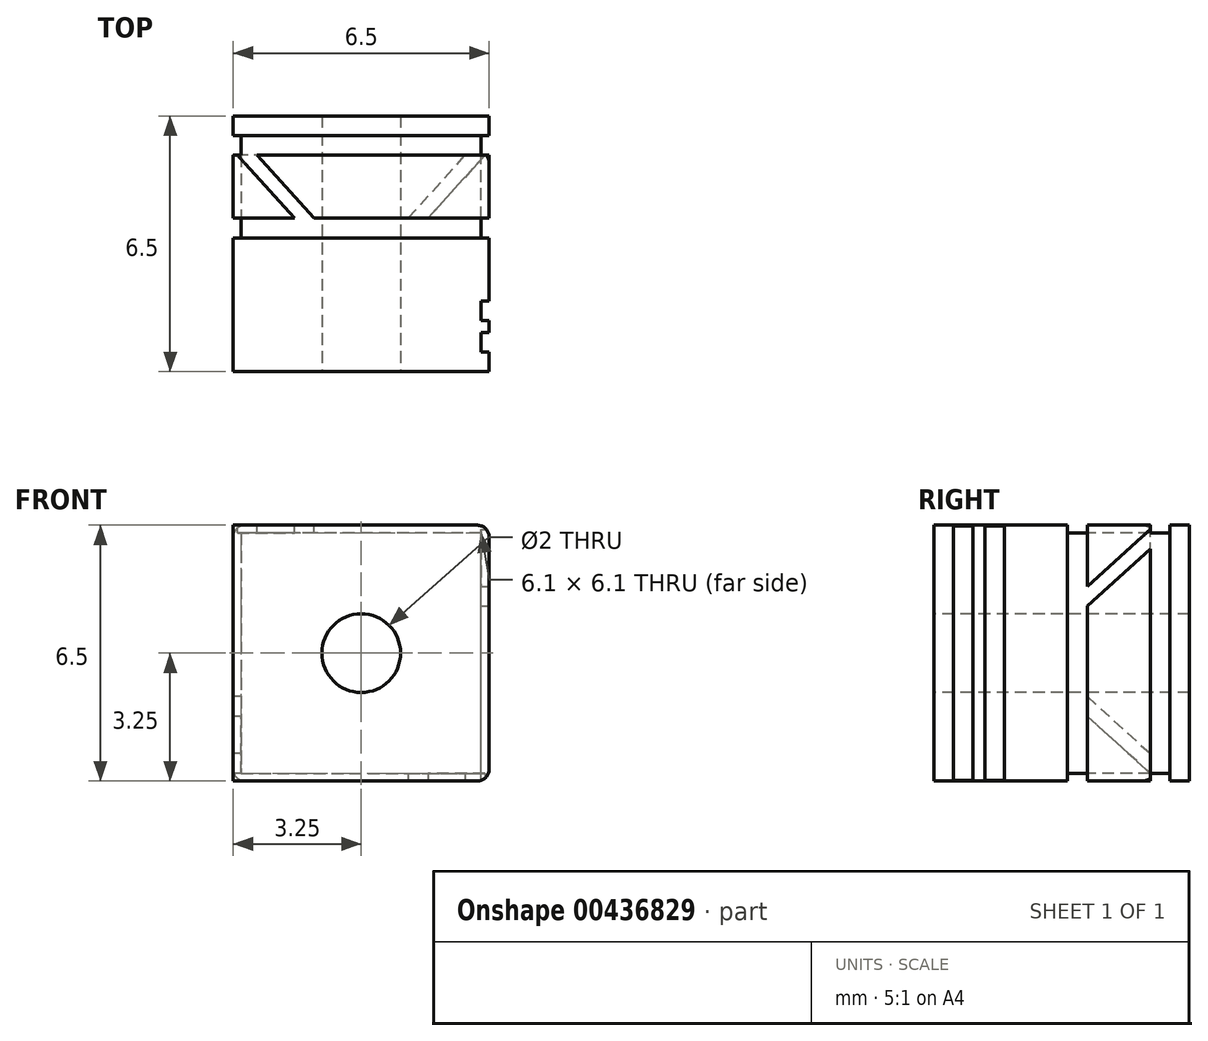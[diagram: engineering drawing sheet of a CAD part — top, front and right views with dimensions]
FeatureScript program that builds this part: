
annotation { "Feature Type Name" : "Feature", "Feature Type Description" : "" }
export const myFeature = defineFeature(function(context is Context, id is Id, definition is map)
    precondition{}
    {
        {
            var Q0;
            Q0=qCreatedBy(makeId("Front.planeOp"),FACE);
            var sketch = newSketch(context, id + "F0", { "sketchPlane" : qUnion([Q0])});
            skLineSegment(sketch, "E0.bottom", {"start": v(0, 0) * mm, "end": v(6.5, 0) * mm});
            skLineSegment(sketch, "E0.top", {"start": v(0, -6.5) * mm, "end": v(6.5, -6.5) * mm});
            skLineSegment(sketch, "E0.left", {"start": v(0, 0) * mm, "end": v(0, -6.5) * mm});
            skLineSegment(sketch, "E0.right", {"start": v(6.5, 0) * mm, "end": v(6.5, -6.5) * mm});
            skSolve(sketch);
        }
        {
            var Q0;
            Q0=makeQuery(id+"F0.imprint","IMPRINT",FACE,{"disambiguationData":[TD([[makeQuery(id+"F0.imprint","IMPRINT",EDGE,{"derivedFrom":sQuery(id+"F0.wireOp",EDGE,"E0.bottom")}),-1.0]])]});
            extrude(context, id + "F1", {"entities" : qUnion([Q0]), "depth" : 6.5 * mm});
        }
        {
            var Q0;
            Q0=makeQuery(id+"F1.opExtrude","CAP_FACE",FACE,{"disambiguationData":[OSD([sQuery(id+"F0.wireOp",EDGE,"E0.bottom"),sQuery(id+"F0.wireOp",EDGE,"E0.top"),sQuery(id+"F0.wireOp",EDGE,"E0.left"),sQuery(id+"F0.wireOp",EDGE,"E0.right")])],"isStart":false});
            var sketch = newSketch(context, id + "F2", { "sketchPlane" : qUnion([Q0])});
            skCircle(sketch, "E1", {"center": v(3.25, -3.25) * mm, "radius": 1 * mm});
            skPoint(sketch, "E1.centerSnap0", {"position": v(3.25, -6.5) * mm});
            skPoint(sketch, "E1.centerSnap1", {"position": v(0, -3.25) * mm});
            skLineSegment(sketch, "E2", {"start": v(0.3, 0) * mm, "end": v(0.3, -6.5) * mm});
            skLineSegment(sketch, "E3", {"start": v(0.45, -6.5) * mm, "end": v(0.45, 0) * mm});
            skSolve(sketch);
        }
        {
            var Q0;
            Q0=makeQuery(id+"F2.imprint","IMPRINT",FACE,{"disambiguationData":[TD([[makeQuery(id+"F2.imprint","IMPRINT",EDGE,{"derivedFrom":sQuery(id+"F2.wireOp",EDGE,"E1")}),1.0]])]});
            extrude(context, id + "F3", {"entities" : qUnion([Q0]), "operationType" : NewBodyOperationType.REMOVE, "oppositeDirection" : true, "depth" : 25 * mm});
        }
        {
            var Q0;
            Q0=makeQuery(id+"F1.opExtrude","SWEPT_FACE",FACE,{"disambiguationData":[OSD([sQuery(id+"F0.wireOp",EDGE,"E0.right")])]});
            var sketch = newSketch(context, id + "F4", { "sketchPlane" : qUnion([Q0])});
            skLineSegment(sketch, "E4", {"start": v(-6, -6.5) * mm, "end": v(-6, 0) * mm});
            skLineSegment(sketch, "E5", {"start": v(-0.5, -6.5) * mm, "end": v(-0.5, 0) * mm});
            skLineSegment(sketch, "E6.bottom", {"start": v(-5.5, -6.5) * mm, "end": v(-5.2, -6.5) * mm});
            skLineSegment(sketch, "E6.top", {"start": v(-5.5, 0) * mm, "end": v(-5.2, 0) * mm});
            skLineSegment(sketch, "E6.left", {"start": v(-5.5, -6.5) * mm, "end": v(-5.5, 0) * mm});
            skLineSegment(sketch, "E6.right", {"start": v(-5.2, -6.5) * mm, "end": v(-5.2, 0) * mm});
            skLineSegment(sketch, "E7.bottom", {"start": v(-4.7, -6.5) * mm, "end": v(-3.1, -6.5) * mm});
            skLineSegment(sketch, "E7.top", {"start": v(-4.7, 0) * mm, "end": v(-3.1, 0) * mm});
            skLineSegment(sketch, "E7.left", {"start": v(-4.7, -6.5) * mm, "end": v(-4.7, 0) * mm});
            skLineSegment(sketch, "E7.right", {"start": v(-3.1, -6.5) * mm, "end": v(-3.1, 0) * mm});
            skLineSegment(sketch, "E8.bottom", {"start": v(-2.6, -6.5) * mm, "end": v(-1, -6.5) * mm});
            skLineSegment(sketch, "E8.top", {"start": v(-2.6, 0) * mm, "end": v(-1, 0) * mm});
            skLineSegment(sketch, "E8.left", {"start": v(-2.6, -6.5) * mm, "end": v(-2.6, -2.06) * mm});
            skLineSegment(sketch, "E8.right", {"start": v(-1, -6.5) * mm, "end": v(-1, -0.6) * mm});
            skLineSegment(sketch, "E9", {"start": v(-1, -0.1) * mm, "end": v(-2.6, -1.56) * mm});
            skLineSegment(sketch, "E10", {"start": v(-2.6, -2.06) * mm, "end": v(-1, -0.6) * mm});
            skLineSegment(sketch, "E11.trimOffspring", {"start": v(-2.6, -1.56) * mm, "end": v(-2.6, 0) * mm});
            skLineSegment(sketch, "E12.trimOffspring", {"start": v(-1, -0.1) * mm, "end": v(-1, 0) * mm});
            skSolve(sketch);
        }
        {
            var Q0;
            {var subQ0=sQuery(id+"F4.wireOp",EDGE,"E4");Q0=makeQuery(id+"F4.imprint","IMPRINT",FACE,{"disambiguationData":[TD([[makeQuery(id+"F4.imprint","IMPRINT",EDGE,{"derivedFrom":subQ0}),-1.0]])]});}
            var Q1;
            {var subQ0=sQuery(id+"F4.wireOp",EDGE,"E6.right");Q1=makeQuery(id+"F4.imprint","IMPRINT",FACE,{"disambiguationData":[TD([[makeQuery(id+"F4.imprint","IMPRINT",EDGE,{"derivedFrom":subQ0}),-1.0]])]});}
            var Q2;
            {var subQ6=sQuery(id+"F4.wireOp",EDGE,"E5");Q2=makeQuery(id+"F4.imprint","IMPRINT",FACE,{"disambiguationData":[TD([[makeQuery(id+"F4.imprint","IMPRINT",EDGE,{"derivedFrom":subQ6}),1.0]])]});}
            extrude(context, id + "F5", {"entities" : qUnion([Q0, Q1, Q2]), "operationType" : NewBodyOperationType.REMOVE, "oppositeDirection" : true, "depth" : 0.2 * mm});
        }
        {
            var Q0;
            Q0=makeQuery(id+"F1.opExtrude","SWEPT_FACE",FACE,{"disambiguationData":[OSD([sQuery(id+"F0.wireOp",EDGE,"E0.bottom")])]});
            var sketch = newSketch(context, id + "F6", { "sketchPlane" : qUnion([Q0])});
            skLineSegment(sketch, "E13", {"start": v(6.5, -6) * mm, "end": v(0, -6) * mm});
            skLineSegment(sketch, "E14", {"start": v(6.5, -0.5) * mm, "end": v(0, -0.5) * mm});
            skLineSegment(sketch, "E15.bottom", {"start": v(6.5, -5.5) * mm, "end": v(6.5, -5.2) * mm});
            skLineSegment(sketch, "E15.top", {"start": v(0, -5.5) * mm, "end": v(0, -5.2) * mm});
            skLineSegment(sketch, "E15.left", {"start": v(6.5, -5.5) * mm, "end": v(0, -5.5) * mm});
            skLineSegment(sketch, "E15.right", {"start": v(6.5, -5.2) * mm, "end": v(0, -5.2) * mm});
            skLineSegment(sketch, "E16.bottom", {"start": v(6.5, -4.7) * mm, "end": v(6.5, -3.1) * mm});
            skLineSegment(sketch, "E16.top", {"start": v(0, -4.7) * mm, "end": v(0, -3.1) * mm});
            skLineSegment(sketch, "E16.left", {"start": v(6.5, -4.7) * mm, "end": v(0, -4.7) * mm});
            skLineSegment(sketch, "E16.right", {"start": v(6.5, -3.1) * mm, "end": v(0, -3.1) * mm});
            skLineSegment(sketch, "E17.bottom", {"start": v(6.5, -2.6) * mm, "end": v(6.5, -1) * mm});
            skLineSegment(sketch, "E17.top", {"start": v(0, -2.6) * mm, "end": v(0, -1) * mm});
            skLineSegment(sketch, "E17.left", {"start": v(6.5, -2.6) * mm, "end": v(2.06, -2.6) * mm});
            skLineSegment(sketch, "E17.right", {"start": v(6.5, -1) * mm, "end": v(0.6, -1) * mm});
            skLineSegment(sketch, "E18", {"start": v(0.1, -1) * mm, "end": v(1.56, -2.6) * mm});
            skLineSegment(sketch, "E19", {"start": v(2.06, -2.6) * mm, "end": v(0.6, -1) * mm});
            skLineSegment(sketch, "E20.trimOffspring", {"start": v(1.56, -2.6) * mm, "end": v(0, -2.6) * mm});
            skLineSegment(sketch, "E21.trimOffspring", {"start": v(0.1, -1) * mm, "end": v(0, -1) * mm});
            skSolve(sketch);
        }
        {
            var Q0;
            {var subQ1=sQuery(id+"F0.wireOp",EDGE,"E0.right");var subQ2=sQuery(id+"F0.wireOp",EDGE,"E0.bottom");var subQ3=makeQuery(id+"F1.opExtrude","SWEPT_EDGE",EDGE,{"disambiguationData":[OSD([subQ2,subQ1])]});var subQ4=makeQuery(id+"F5.boolean.opBoolean","COPY",EDGE,{"derivedFrom":makeQuery(id+"F5.opExtrude","CAP_EDGE",EDGE,{"disambiguationData":[OSD([subQ2,subQ1]),TDD([makeQuery(id+"F4.imprint","IMPRINT",EDGE,{"disambiguationData":[TD([[makeQuery(id+"F4.imprint","INTERSECT",VERTEX,{"derivedFrom":[subQ3,sQuery(id+"F4.wireOp",EDGE,"E4")]}),-1.0]])],"derivedFrom":subQ3})])],"isStart":false})});Q0=makeQuery(id+"F6.imprint","IMPRINT",FACE,{"disambiguationData":[TD([[makeQuery(id+"F6.imprint","IMPRINT",EDGE,{"derivedFrom":subQ4}),1.0]])]});}
            var Q1;
            {var subQ1=sQuery(id+"F0.wireOp",EDGE,"E0.right");var subQ2=sQuery(id+"F0.wireOp",EDGE,"E0.bottom");var subQ3=makeQuery(id+"F1.opExtrude","SWEPT_EDGE",EDGE,{"disambiguationData":[OSD([subQ2,subQ1])]});var subQ4=makeQuery(id+"F5.boolean.opBoolean","COPY",EDGE,{"derivedFrom":makeQuery(id+"F5.opExtrude","CAP_EDGE",EDGE,{"disambiguationData":[OSD([subQ2,subQ1]),TDD([makeQuery(id+"F4.imprint","IMPRINT",EDGE,{"disambiguationData":[TD([[makeQuery(id+"F4.imprint","INTERSECT",VERTEX,{"derivedFrom":[subQ3,sQuery(id+"F4.wireOp",EDGE,"E6.top"),sQuery(id+"F4.wireOp",EDGE,"E6.right")]}),-1.0]])],"derivedFrom":subQ3})])],"isStart":false})});Q1=makeQuery(id+"F6.imprint","IMPRINT",FACE,{"disambiguationData":[TD([[makeQuery(id+"F6.imprint","IMPRINT",EDGE,{"derivedFrom":subQ4}),1.0]])]});}
            var Q2;
            Q2=makeQuery(id+"F6.imprint","IMPRINT",FACE,{"disambiguationData":[TD([[makeQuery(id+"F6.imprint","IMPRINT",EDGE,{"derivedFrom":sQuery(id+"F6.wireOp",EDGE,"E18")}),1.0]])]});
            extrude(context, id + "F7", {"entities" : qUnion([Q0, Q1, Q2]), "operationType" : NewBodyOperationType.REMOVE, "oppositeDirection" : true, "depth" : 0.2 * mm});
        }
        {
            var Q0;
            Q0=makeQuery(id+"F1.opExtrude","SWEPT_FACE",FACE,{"disambiguationData":[OSD([sQuery(id+"F0.wireOp",EDGE,"E0.left")])]});
            var sketch = newSketch(context, id + "F8", { "sketchPlane" : qUnion([Q0])});
            skLineSegment(sketch, "E22", {"start": v(6, 0) * mm, "end": v(6, -6.5) * mm});
            skLineSegment(sketch, "E23", {"start": v(0.5, 0) * mm, "end": v(0.5, -6.5) * mm});
            skLineSegment(sketch, "E24.bottom", {"start": v(5.5, 0) * mm, "end": v(5.2, 0) * mm});
            skLineSegment(sketch, "E24.top", {"start": v(5.5, -6.5) * mm, "end": v(5.2, -6.5) * mm});
            skLineSegment(sketch, "E24.left", {"start": v(5.5, 0) * mm, "end": v(5.5, -6.5) * mm});
            skLineSegment(sketch, "E24.right", {"start": v(5.2, 0) * mm, "end": v(5.2, -6.5) * mm});
            skLineSegment(sketch, "E25.bottom", {"start": v(4.7, 0) * mm, "end": v(3.1, 0) * mm});
            skLineSegment(sketch, "E25.top", {"start": v(4.7, -6.5) * mm, "end": v(3.1, -6.5) * mm});
            skLineSegment(sketch, "E25.left", {"start": v(4.7, 0) * mm, "end": v(4.7, -6.5) * mm});
            skLineSegment(sketch, "E25.right", {"start": v(3.1, 0) * mm, "end": v(3.1, -6.5) * mm});
            skLineSegment(sketch, "E26.bottom", {"start": v(2.6, 0) * mm, "end": v(1, 0) * mm});
            skLineSegment(sketch, "E26.top", {"start": v(2.6, -6.5) * mm, "end": v(1, -6.5) * mm});
            skLineSegment(sketch, "E26.left", {"start": v(2.6, 0) * mm, "end": v(2.6, -4.35) * mm});
            skLineSegment(sketch, "E26.right", {"start": v(1, 0) * mm, "end": v(1, -5.8) * mm});
            skLineSegment(sketch, "E27", {"start": v(1, -6.3) * mm, "end": v(2.6, -4.85) * mm});
            skLineSegment(sketch, "E28", {"start": v(2.6, -4.35) * mm, "end": v(1, -5.8) * mm});
            skLineSegment(sketch, "E29.trimOffspring", {"start": v(2.6, -4.85) * mm, "end": v(2.6, -6.5) * mm});
            skLineSegment(sketch, "E30.trimOffspring", {"start": v(1, -6.3) * mm, "end": v(1, -6.5) * mm});
            skSolve(sketch);
        }
        {
            var Q0;
            {var subQ1=sQuery(id+"F0.wireOp",EDGE,"E0.left");var subQ2=sQuery(id+"F0.wireOp",EDGE,"E0.bottom");var subQ3=makeQuery(id+"F1.opExtrude","SWEPT_EDGE",EDGE,{"disambiguationData":[OSD([subQ2,subQ1])]});var subQ4=makeQuery(id+"F7.boolean.opBoolean","COPY",EDGE,{"derivedFrom":makeQuery(id+"F7.opExtrude","CAP_EDGE",EDGE,{"disambiguationData":[OSD([subQ2,subQ1]),TDD([makeQuery(id+"F6.imprint","IMPRINT",EDGE,{"disambiguationData":[TD([[makeQuery(id+"F6.imprint","INTERSECT",VERTEX,{"derivedFrom":[subQ3,sQuery(id+"F6.wireOp",EDGE,"E13")]}),-1.0]])],"derivedFrom":subQ3})])],"isStart":false})});Q0=makeQuery(id+"F8.imprint","IMPRINT",FACE,{"disambiguationData":[TD([[makeQuery(id+"F8.imprint","IMPRINT",EDGE,{"derivedFrom":subQ4}),1.0]])]});}
            var Q1;
            {var subQ1=sQuery(id+"F0.wireOp",EDGE,"E0.left");var subQ2=sQuery(id+"F0.wireOp",EDGE,"E0.bottom");var subQ3=makeQuery(id+"F1.opExtrude","SWEPT_EDGE",EDGE,{"disambiguationData":[OSD([subQ2,subQ1])]});var subQ4=makeQuery(id+"F7.boolean.opBoolean","COPY",EDGE,{"derivedFrom":makeQuery(id+"F7.opExtrude","CAP_EDGE",EDGE,{"disambiguationData":[OSD([subQ2,subQ1]),TDD([makeQuery(id+"F6.imprint","IMPRINT",EDGE,{"disambiguationData":[TD([[makeQuery(id+"F6.imprint","INTERSECT",VERTEX,{"derivedFrom":[subQ3,sQuery(id+"F6.wireOp",EDGE,"E15.top"),sQuery(id+"F6.wireOp",EDGE,"E15.right")]}),-1.0]])],"derivedFrom":subQ3})])],"isStart":false})});Q1=makeQuery(id+"F8.imprint","IMPRINT",FACE,{"disambiguationData":[TD([[makeQuery(id+"F8.imprint","IMPRINT",EDGE,{"derivedFrom":subQ4}),1.0]])]});}
            var Q2;
            Q2=makeQuery(id+"F8.imprint","IMPRINT",FACE,{"disambiguationData":[TD([[makeQuery(id+"F8.imprint","IMPRINT",EDGE,{"derivedFrom":sQuery(id+"F8.wireOp",EDGE,"E27")}),1.0]])]});
            extrude(context, id + "F9", {"entities" : qUnion([Q0, Q1, Q2]), "operationType" : NewBodyOperationType.REMOVE, "oppositeDirection" : true, "depth" : 0.2 * mm});
        }
        {
            var Q0;
            Q0=makeQuery(id+"F1.opExtrude","SWEPT_FACE",FACE,{"disambiguationData":[OSD([sQuery(id+"F0.wireOp",EDGE,"E0.top")])]});
            var sketch = newSketch(context, id + "F10", { "sketchPlane" : qUnion([Q0])});
            skLineSegment(sketch, "E31", {"start": v(0, 6) * mm, "end": v(6.5, 6) * mm});
            skLineSegment(sketch, "E32", {"start": v(0, 0.5) * mm, "end": v(6.5, 0.5) * mm});
            skLineSegment(sketch, "E33.bottom", {"start": v(0, 5.5) * mm, "end": v(0, 5.2) * mm});
            skLineSegment(sketch, "E33.top", {"start": v(6.5, 5.5) * mm, "end": v(6.5, 5.2) * mm});
            skLineSegment(sketch, "E33.left", {"start": v(0, 5.5) * mm, "end": v(6.5, 5.5) * mm});
            skLineSegment(sketch, "E33.right", {"start": v(0, 5.2) * mm, "end": v(6.5, 5.2) * mm});
            skLineSegment(sketch, "E34.bottom", {"start": v(0, 4.7) * mm, "end": v(0, 3.1) * mm});
            skLineSegment(sketch, "E34.top", {"start": v(6.5, 4.7) * mm, "end": v(6.5, 3.1) * mm});
            skLineSegment(sketch, "E34.left", {"start": v(0, 4.7) * mm, "end": v(6.5, 4.7) * mm});
            skLineSegment(sketch, "E34.right", {"start": v(0, 3.1) * mm, "end": v(6.5, 3.1) * mm});
            skLineSegment(sketch, "E35.bottom", {"start": v(0, 2.6) * mm, "end": v(0, 1) * mm});
            skLineSegment(sketch, "E35.top", {"start": v(6.5, 2.6) * mm, "end": v(6.5, 1) * mm});
            skLineSegment(sketch, "E35.left", {"start": v(0, 2.6) * mm, "end": v(4.44, 2.6) * mm});
            skLineSegment(sketch, "E35.right", {"start": v(0, 1) * mm, "end": v(5.9, 1) * mm});
            skLineSegment(sketch, "E36", {"start": v(6.4, 1) * mm, "end": v(4.94, 2.6) * mm});
            skLineSegment(sketch, "E37", {"start": v(4.44, 2.6) * mm, "end": v(5.9, 1) * mm});
            skLineSegment(sketch, "E38.trimOffspring", {"start": v(4.94, 2.6) * mm, "end": v(6.5, 2.6) * mm});
            skLineSegment(sketch, "E39.trimOffspring", {"start": v(6.4, 1) * mm, "end": v(6.5, 1) * mm});
            skSolve(sketch);
        }
        {
            var Q0;
            {var subQ1=sQuery(id+"F0.wireOp",EDGE,"E0.right");var subQ2=sQuery(id+"F0.wireOp",EDGE,"E0.top");var subQ3=makeQuery(id+"F1.opExtrude","SWEPT_EDGE",EDGE,{"disambiguationData":[OSD([subQ2,subQ1])]});var subQ4=makeQuery(id+"F5.boolean.opBoolean","COPY",EDGE,{"derivedFrom":makeQuery(id+"F5.opExtrude","CAP_EDGE",EDGE,{"disambiguationData":[OSD([subQ2,subQ1]),TDD([makeQuery(id+"F4.imprint","IMPRINT",EDGE,{"disambiguationData":[TD([[makeQuery(id+"F4.imprint","INTERSECT",VERTEX,{"derivedFrom":[subQ3,sQuery(id+"F4.wireOp",EDGE,"E4")]}),-1.0]])],"derivedFrom":subQ3})])],"isStart":false})});Q0=makeQuery(id+"F10.imprint","IMPRINT",FACE,{"disambiguationData":[TD([[makeQuery(id+"F10.imprint","IMPRINT",EDGE,{"derivedFrom":subQ4}),-1.0]])]});}
            var Q1;
            {var subQ1=sQuery(id+"F0.wireOp",EDGE,"E0.right");var subQ2=sQuery(id+"F0.wireOp",EDGE,"E0.top");var subQ3=makeQuery(id+"F1.opExtrude","SWEPT_EDGE",EDGE,{"disambiguationData":[OSD([subQ2,subQ1])]});var subQ4=makeQuery(id+"F5.boolean.opBoolean","COPY",EDGE,{"derivedFrom":makeQuery(id+"F5.opExtrude","CAP_EDGE",EDGE,{"disambiguationData":[OSD([subQ2,subQ1]),TDD([makeQuery(id+"F4.imprint","IMPRINT",EDGE,{"disambiguationData":[TD([[makeQuery(id+"F4.imprint","INTERSECT",VERTEX,{"derivedFrom":[subQ3,sQuery(id+"F4.wireOp",EDGE,"E6.bottom"),sQuery(id+"F4.wireOp",EDGE,"E6.right")]}),-1.0]])],"derivedFrom":subQ3})])],"isStart":false})});Q1=makeQuery(id+"F10.imprint","IMPRINT",FACE,{"disambiguationData":[TD([[makeQuery(id+"F10.imprint","IMPRINT",EDGE,{"derivedFrom":subQ4}),-1.0]])]});}
            var Q2;
            {var subQ6=sQuery(id+"F10.wireOp",EDGE,"E36");Q2=makeQuery(id+"F10.imprint","IMPRINT",FACE,{"disambiguationData":[TD([[makeQuery(id+"F10.imprint","IMPRINT",EDGE,{"derivedFrom":subQ6}),1.0]])]});}
            extrude(context, id + "F11", {"entities" : qUnion([Q0, Q1, Q2]), "operationType" : NewBodyOperationType.REMOVE, "oppositeDirection" : true, "depth" : 0.2 * mm});
        }
        {
            var Q0;
            {var subQ0=sQuery(id+"F0.wireOp",EDGE,"E0.left");var subQ1=sQuery(id+"F0.wireOp",EDGE,"E0.top");Q0=makeQuery(id+"F9.boolean.opBoolean","SPLIT",EDGE,{"disambiguationData":[TD([makeQuery(id+"F5.boolean.opBoolean","COPY",FACE,{"derivedFrom":makeQuery(id+"F5.opExtrude","SWEPT_FACE",FACE,{"disambiguationData":[OSD([sQuery(id+"F4.wireOp",EDGE,"E4")])]})})])],"derivedFrom":makeQuery(id+"F1.opExtrude","SWEPT_EDGE",EDGE,{"disambiguationData":[OSD([subQ1,subQ0])]})});}
            var Q1;
            {var subQ0=sQuery(id+"F0.wireOp",EDGE,"E0.left");var subQ1=sQuery(id+"F0.wireOp",EDGE,"E0.top");var subQ2=makeQuery(id+"F1.opExtrude","SWEPT_EDGE",EDGE,{"disambiguationData":[OSD([subQ1,subQ0])]});Q1=makeQuery(id+"F11.boolean.opBoolean","COPY",EDGE,{"derivedFrom":makeQuery(id+"F11.opExtrude","CAP_EDGE",EDGE,{"disambiguationData":[OSD([subQ1,subQ0]),TDD([makeQuery(id+"F10.imprint","IMPRINT",EDGE,{"derivedFrom":makeQuery(id+"F9.boolean.opBoolean","COPY",EDGE,{"derivedFrom":makeQuery(id+"F9.opExtrude","CAP_EDGE",EDGE,{"disambiguationData":[OSD([subQ1,subQ0]),TDD([makeQuery(id+"F8.imprint","IMPRINT",EDGE,{"disambiguationData":[TD([[makeQuery(id+"F8.imprint","INTERSECT",VERTEX,{"derivedFrom":[subQ2,sQuery(id+"F8.wireOp",EDGE,"E22")]}),-1.0]])],"derivedFrom":subQ2})])],"isStart":false})})})])],"isStart":false})});}
            var Q2;
            {var subQ0=sQuery(id+"F0.wireOp",EDGE,"E0.left");var subQ1=sQuery(id+"F0.wireOp",EDGE,"E0.top");var subQ2=makeQuery(id+"F1.opExtrude","SWEPT_EDGE",EDGE,{"disambiguationData":[OSD([subQ1,subQ0])]});Q2=makeQuery(id+"F11.boolean.opBoolean","COPY",EDGE,{"derivedFrom":makeQuery(id+"F11.opExtrude","CAP_EDGE",EDGE,{"disambiguationData":[OSD([subQ1,subQ0]),TDD([makeQuery(id+"F10.imprint","IMPRINT",EDGE,{"derivedFrom":makeQuery(id+"F9.boolean.opBoolean","COPY",EDGE,{"derivedFrom":makeQuery(id+"F9.opExtrude","CAP_EDGE",EDGE,{"disambiguationData":[OSD([subQ1,subQ0]),TDD([makeQuery(id+"F8.imprint","IMPRINT",EDGE,{"disambiguationData":[TD([[makeQuery(id+"F8.imprint","INTERSECT",VERTEX,{"derivedFrom":[subQ2,sQuery(id+"F8.wireOp",EDGE,"E24.top"),sQuery(id+"F8.wireOp",EDGE,"E24.right")]}),-1.0]])],"derivedFrom":subQ2})])],"isStart":false})})})])],"isStart":false})});}
            var Q3;
            {var subQ0=sQuery(id+"F0.wireOp",EDGE,"E0.top");var subQ1=sQuery(id+"F0.wireOp",EDGE,"E0.left");Q3=makeQuery(id+"F9.boolean.opBoolean","SPLIT",EDGE,{"disambiguationData":[TD([makeQuery(id+"F5.boolean.opBoolean","COPY",FACE,{"derivedFrom":makeQuery(id+"F5.opExtrude","SWEPT_FACE",FACE,{"disambiguationData":[OSD([sQuery(id+"F4.wireOp",EDGE,"E6.left")])]})})])],"derivedFrom":makeQuery(id+"F1.opExtrude","SWEPT_EDGE",EDGE,{"disambiguationData":[OSD([subQ0,subQ1])]})});}
            var Q4;
            {var subQ0=sQuery(id+"F0.wireOp",EDGE,"E0.left");var subQ1=sQuery(id+"F0.wireOp",EDGE,"E0.top");Q4=makeQuery(id+"F9.boolean.opBoolean","SPLIT",EDGE,{"disambiguationData":[TD([makeQuery(id+"F5.boolean.opBoolean","COPY",FACE,{"derivedFrom":makeQuery(id+"F5.opExtrude","SWEPT_FACE",FACE,{"disambiguationData":[OSD([sQuery(id+"F4.wireOp",EDGE,"E7.left")])]})})])],"derivedFrom":makeQuery(id+"F1.opExtrude","SWEPT_EDGE",EDGE,{"disambiguationData":[OSD([subQ1,subQ0])]})});}
            var Q5;
            {var subQ0=sQuery(id+"F0.wireOp",EDGE,"E0.left");var subQ1=sQuery(id+"F0.wireOp",EDGE,"E0.top");var subQ2=makeQuery(id+"F1.opExtrude","SWEPT_EDGE",EDGE,{"disambiguationData":[OSD([subQ1,subQ0])]});Q5=makeQuery(id+"F11.boolean.opBoolean","COPY",EDGE,{"derivedFrom":makeQuery(id+"F11.opExtrude","CAP_EDGE",EDGE,{"disambiguationData":[OSD([subQ1,subQ0]),TDD([makeQuery(id+"F10.imprint","IMPRINT",EDGE,{"derivedFrom":makeQuery(id+"F9.boolean.opBoolean","COPY",EDGE,{"derivedFrom":makeQuery(id+"F9.opExtrude","CAP_EDGE",EDGE,{"disambiguationData":[OSD([subQ1,subQ0]),TDD([makeQuery(id+"F8.imprint","IMPRINT",EDGE,{"disambiguationData":[TD([[makeQuery(id+"F8.imprint","INTERSECT",VERTEX,{"derivedFrom":[subQ2,sQuery(id+"F8.wireOp",EDGE,"E29.trimOffspring")]}),1.0]])],"derivedFrom":subQ2})])],"isStart":false})})})])],"isStart":false})});}
            var Q6;
            {var subQ0=sQuery(id+"F0.wireOp",EDGE,"E0.top");var subQ1=sQuery(id+"F0.wireOp",EDGE,"E0.left");Q6=makeQuery(id+"F9.boolean.opBoolean","SPLIT",EDGE,{"disambiguationData":[TD([makeQuery(id+"F9.opExtrude","SWEPT_FACE",FACE,{"disambiguationData":[OSD([sQuery(id+"F8.wireOp",EDGE,"E29.trimOffspring")])]})])],"derivedFrom":makeQuery(id+"F1.opExtrude","SWEPT_EDGE",EDGE,{"disambiguationData":[OSD([subQ0,subQ1])]})});}
            var Q7;
            {var subQ0=sQuery(id+"F0.wireOp",EDGE,"E0.left");var subQ1=sQuery(id+"F0.wireOp",EDGE,"E0.top");var subQ2=makeQuery(id+"F1.opExtrude","SWEPT_EDGE",EDGE,{"disambiguationData":[OSD([subQ1,subQ0])]});Q7=makeQuery(id+"F11.boolean.opBoolean","COPY",EDGE,{"derivedFrom":makeQuery(id+"F11.opExtrude","CAP_EDGE",EDGE,{"disambiguationData":[OSD([subQ1,subQ0]),TDD([makeQuery(id+"F10.imprint","IMPRINT",EDGE,{"derivedFrom":makeQuery(id+"F9.boolean.opBoolean","COPY",EDGE,{"derivedFrom":makeQuery(id+"F9.opExtrude","CAP_EDGE",EDGE,{"disambiguationData":[OSD([subQ1,subQ0]),TDD([makeQuery(id+"F8.imprint","IMPRINT",EDGE,{"disambiguationData":[TD([[makeQuery(id+"F8.imprint","INTERSECT",VERTEX,{"derivedFrom":[subQ2,sQuery(id+"F8.wireOp",EDGE,"E23")]}),1.0]])],"derivedFrom":subQ2})])],"isStart":false})})})])],"isStart":false})});}
            var Q8;
            {var subQ0=sQuery(id+"F0.wireOp",EDGE,"E0.left");var subQ1=sQuery(id+"F0.wireOp",EDGE,"E0.top");Q8=makeQuery(id+"F9.boolean.opBoolean","SPLIT",EDGE,{"disambiguationData":[TD([makeQuery(id+"F5.boolean.opBoolean","COPY",FACE,{"derivedFrom":makeQuery(id+"F5.opExtrude","SWEPT_FACE",FACE,{"disambiguationData":[OSD([sQuery(id+"F4.wireOp",EDGE,"E5")])]})})])],"derivedFrom":makeQuery(id+"F1.opExtrude","SWEPT_EDGE",EDGE,{"disambiguationData":[OSD([subQ1,subQ0])]})});}
            var Q9;
            {var subQ0=sQuery(id+"F0.wireOp",EDGE,"E0.right");var subQ1=sQuery(id+"F0.wireOp",EDGE,"E0.top");Q9=makeQuery(id+"F5.boolean.opBoolean","SPLIT",EDGE,{"disambiguationData":[TD([makeQuery(id+"F5.opExtrude","SWEPT_FACE",FACE,{"disambiguationData":[OSD([sQuery(id+"F4.wireOp",EDGE,"E5")])]})])],"derivedFrom":makeQuery(id+"F1.opExtrude","SWEPT_EDGE",EDGE,{"disambiguationData":[OSD([subQ1,subQ0])]})});}
            var Q10;
            {var subQ0=sQuery(id+"F0.wireOp",EDGE,"E0.right");var subQ1=sQuery(id+"F0.wireOp",EDGE,"E0.top");var subQ2=makeQuery(id+"F1.opExtrude","SWEPT_EDGE",EDGE,{"disambiguationData":[OSD([subQ1,subQ0])]});Q10=makeQuery(id+"F11.boolean.opBoolean","COPY",EDGE,{"derivedFrom":makeQuery(id+"F11.opExtrude","CAP_EDGE",EDGE,{"disambiguationData":[OSD([subQ1,subQ0]),TDD([makeQuery(id+"F10.imprint","IMPRINT",EDGE,{"derivedFrom":makeQuery(id+"F5.boolean.opBoolean","COPY",EDGE,{"derivedFrom":makeQuery(id+"F5.opExtrude","CAP_EDGE",EDGE,{"disambiguationData":[OSD([subQ1,subQ0]),TDD([makeQuery(id+"F4.imprint","IMPRINT",EDGE,{"disambiguationData":[TD([[makeQuery(id+"F4.imprint","INTERSECT",VERTEX,{"derivedFrom":[subQ2,sQuery(id+"F4.wireOp",EDGE,"E5")]}),1.0]])],"derivedFrom":subQ2})])],"isStart":false})})})])],"isStart":false})});}
            var Q11;
            {var subQ0=sQuery(id+"F0.wireOp",EDGE,"E0.top");var subQ1=sQuery(id+"F0.wireOp",EDGE,"E0.right");Q11=makeQuery(id+"F5.boolean.opBoolean","SPLIT",EDGE,{"disambiguationData":[TD([makeQuery(id+"F5.opExtrude","SWEPT_FACE",FACE,{"disambiguationData":[OSD([sQuery(id+"F4.wireOp",EDGE,"E8.left")])]})])],"derivedFrom":makeQuery(id+"F1.opExtrude","SWEPT_EDGE",EDGE,{"disambiguationData":[OSD([subQ0,subQ1])]})});}
            var Q12;
            {var subQ0=sQuery(id+"F0.wireOp",EDGE,"E0.right");var subQ1=sQuery(id+"F0.wireOp",EDGE,"E0.top");var subQ2=makeQuery(id+"F1.opExtrude","SWEPT_EDGE",EDGE,{"disambiguationData":[OSD([subQ1,subQ0])]});Q12=makeQuery(id+"F11.boolean.opBoolean","COPY",EDGE,{"derivedFrom":makeQuery(id+"F11.opExtrude","CAP_EDGE",EDGE,{"disambiguationData":[OSD([subQ1,subQ0]),TDD([makeQuery(id+"F10.imprint","IMPRINT",EDGE,{"derivedFrom":makeQuery(id+"F5.boolean.opBoolean","COPY",EDGE,{"derivedFrom":makeQuery(id+"F5.opExtrude","CAP_EDGE",EDGE,{"disambiguationData":[OSD([subQ1,subQ0]),TDD([makeQuery(id+"F4.imprint","IMPRINT",EDGE,{"disambiguationData":[TD([[makeQuery(id+"F4.imprint","INTERSECT",VERTEX,{"derivedFrom":[subQ2,sQuery(id+"F4.wireOp",EDGE,"E7.bottom"),sQuery(id+"F4.wireOp",EDGE,"E7.right")]}),-1.0]])],"derivedFrom":subQ2})])],"isStart":false})})})])],"isStart":false})});}
            var Q13;
            {var subQ0=sQuery(id+"F0.wireOp",EDGE,"E0.top");var subQ1=sQuery(id+"F0.wireOp",EDGE,"E0.right");Q13=makeQuery(id+"F5.boolean.opBoolean","SPLIT",EDGE,{"disambiguationData":[TD([makeQuery(id+"F5.opExtrude","SWEPT_FACE",FACE,{"disambiguationData":[OSD([sQuery(id+"F4.wireOp",EDGE,"E7.left")])]})])],"derivedFrom":makeQuery(id+"F1.opExtrude","SWEPT_EDGE",EDGE,{"disambiguationData":[OSD([subQ0,subQ1])]})});}
            var Q14;
            {var subQ0=sQuery(id+"F0.wireOp",EDGE,"E0.right");var subQ1=sQuery(id+"F0.wireOp",EDGE,"E0.top");var subQ2=makeQuery(id+"F1.opExtrude","SWEPT_EDGE",EDGE,{"disambiguationData":[OSD([subQ1,subQ0])]});Q14=makeQuery(id+"F11.boolean.opBoolean","COPY",EDGE,{"derivedFrom":makeQuery(id+"F11.opExtrude","CAP_EDGE",EDGE,{"disambiguationData":[OSD([subQ1,subQ0]),TDD([makeQuery(id+"F10.imprint","IMPRINT",EDGE,{"derivedFrom":makeQuery(id+"F5.boolean.opBoolean","COPY",EDGE,{"derivedFrom":makeQuery(id+"F5.opExtrude","CAP_EDGE",EDGE,{"disambiguationData":[OSD([subQ1,subQ0]),TDD([makeQuery(id+"F4.imprint","IMPRINT",EDGE,{"disambiguationData":[TD([[makeQuery(id+"F4.imprint","INTERSECT",VERTEX,{"derivedFrom":[subQ2,sQuery(id+"F4.wireOp",EDGE,"E6.bottom"),sQuery(id+"F4.wireOp",EDGE,"E6.right")]}),-1.0]])],"derivedFrom":subQ2})])],"isStart":false})})})])],"isStart":false})});}
            var Q15;
            {var subQ0=sQuery(id+"F0.wireOp",EDGE,"E0.top");var subQ1=sQuery(id+"F0.wireOp",EDGE,"E0.right");Q15=makeQuery(id+"F5.boolean.opBoolean","SPLIT",EDGE,{"disambiguationData":[TD([makeQuery(id+"F5.opExtrude","SWEPT_FACE",FACE,{"disambiguationData":[OSD([sQuery(id+"F4.wireOp",EDGE,"E6.left")])]})])],"derivedFrom":makeQuery(id+"F1.opExtrude","SWEPT_EDGE",EDGE,{"disambiguationData":[OSD([subQ0,subQ1])]})});}
            var Q16;
            {var subQ0=sQuery(id+"F0.wireOp",EDGE,"E0.right");var subQ1=sQuery(id+"F0.wireOp",EDGE,"E0.top");var subQ2=makeQuery(id+"F1.opExtrude","SWEPT_EDGE",EDGE,{"disambiguationData":[OSD([subQ1,subQ0])]});Q16=makeQuery(id+"F11.boolean.opBoolean","COPY",EDGE,{"derivedFrom":makeQuery(id+"F11.opExtrude","CAP_EDGE",EDGE,{"disambiguationData":[OSD([subQ1,subQ0]),TDD([makeQuery(id+"F10.imprint","IMPRINT",EDGE,{"derivedFrom":makeQuery(id+"F5.boolean.opBoolean","COPY",EDGE,{"derivedFrom":makeQuery(id+"F5.opExtrude","CAP_EDGE",EDGE,{"disambiguationData":[OSD([subQ1,subQ0]),TDD([makeQuery(id+"F4.imprint","IMPRINT",EDGE,{"disambiguationData":[TD([[makeQuery(id+"F4.imprint","INTERSECT",VERTEX,{"derivedFrom":[subQ2,sQuery(id+"F4.wireOp",EDGE,"E4")]}),-1.0]])],"derivedFrom":subQ2})])],"isStart":false})})})])],"isStart":false})});}
            var Q17;
            {var subQ0=sQuery(id+"F0.wireOp",EDGE,"E0.right");var subQ1=sQuery(id+"F0.wireOp",EDGE,"E0.top");Q17=makeQuery(id+"F5.boolean.opBoolean","SPLIT",EDGE,{"disambiguationData":[TD([makeQuery(id+"F5.opExtrude","SWEPT_FACE",FACE,{"disambiguationData":[OSD([sQuery(id+"F4.wireOp",EDGE,"E4")])]})])],"derivedFrom":makeQuery(id+"F1.opExtrude","SWEPT_EDGE",EDGE,{"disambiguationData":[OSD([subQ1,subQ0])]})});}
            var Q18;
            {var subQ0=sQuery(id+"F0.wireOp",EDGE,"E0.bottom");var subQ1=sQuery(id+"F0.wireOp",EDGE,"E0.right");Q18=makeQuery(id+"F5.boolean.opBoolean","SPLIT",EDGE,{"disambiguationData":[TD([makeQuery(id+"F5.opExtrude","SWEPT_FACE",FACE,{"disambiguationData":[OSD([sQuery(id+"F4.wireOp",EDGE,"E5")])]})])],"derivedFrom":makeQuery(id+"F1.opExtrude","SWEPT_EDGE",EDGE,{"disambiguationData":[OSD([subQ0,subQ1])]})});}
            var Q19;
            {var subQ0=sQuery(id+"F0.wireOp",EDGE,"E0.right");var subQ1=sQuery(id+"F0.wireOp",EDGE,"E0.bottom");var subQ2=makeQuery(id+"F1.opExtrude","SWEPT_EDGE",EDGE,{"disambiguationData":[OSD([subQ1,subQ0])]});Q19=makeQuery(id+"F7.boolean.opBoolean","COPY",EDGE,{"derivedFrom":makeQuery(id+"F7.opExtrude","CAP_EDGE",EDGE,{"disambiguationData":[OSD([subQ1,subQ0]),TDD([makeQuery(id+"F6.imprint","IMPRINT",EDGE,{"derivedFrom":makeQuery(id+"F5.boolean.opBoolean","COPY",EDGE,{"derivedFrom":makeQuery(id+"F5.opExtrude","CAP_EDGE",EDGE,{"disambiguationData":[OSD([subQ1,subQ0]),TDD([makeQuery(id+"F4.imprint","IMPRINT",EDGE,{"disambiguationData":[TD([[makeQuery(id+"F4.imprint","INTERSECT",VERTEX,{"derivedFrom":[subQ2,sQuery(id+"F4.wireOp",EDGE,"E5")]}),1.0]])],"derivedFrom":subQ2})])],"isStart":false})})})])],"isStart":false})});}
            var Q20;
            {var subQ0=sQuery(id+"F0.wireOp",EDGE,"E0.bottom");var subQ1=sQuery(id+"F0.wireOp",EDGE,"E0.right");Q20=makeQuery(id+"F5.boolean.opBoolean","SPLIT",EDGE,{"disambiguationData":[TD([makeQuery(id+"F5.opExtrude","SWEPT_FACE",FACE,{"disambiguationData":[OSD([sQuery(id+"F4.wireOp",EDGE,"E11.trimOffspring")])]})])],"derivedFrom":makeQuery(id+"F1.opExtrude","SWEPT_EDGE",EDGE,{"disambiguationData":[OSD([subQ0,subQ1])]})});}
            var Q21;
            {var subQ0=sQuery(id+"F0.wireOp",EDGE,"E0.right");var subQ1=sQuery(id+"F0.wireOp",EDGE,"E0.bottom");var subQ2=makeQuery(id+"F1.opExtrude","SWEPT_EDGE",EDGE,{"disambiguationData":[OSD([subQ1,subQ0])]});Q21=makeQuery(id+"F7.boolean.opBoolean","COPY",EDGE,{"derivedFrom":makeQuery(id+"F7.opExtrude","CAP_EDGE",EDGE,{"disambiguationData":[OSD([subQ1,subQ0]),TDD([makeQuery(id+"F6.imprint","IMPRINT",EDGE,{"derivedFrom":makeQuery(id+"F5.boolean.opBoolean","COPY",EDGE,{"derivedFrom":makeQuery(id+"F5.opExtrude","CAP_EDGE",EDGE,{"disambiguationData":[OSD([subQ1,subQ0]),TDD([makeQuery(id+"F4.imprint","IMPRINT",EDGE,{"disambiguationData":[TD([[makeQuery(id+"F4.imprint","INTERSECT",VERTEX,{"derivedFrom":[subQ2,sQuery(id+"F4.wireOp",EDGE,"E7.top"),sQuery(id+"F4.wireOp",EDGE,"E7.right")]}),-1.0]])],"derivedFrom":subQ2})])],"isStart":false})})})])],"isStart":false})});}
            var Q22;
            {var subQ0=sQuery(id+"F0.wireOp",EDGE,"E0.bottom");var subQ1=sQuery(id+"F0.wireOp",EDGE,"E0.right");Q22=makeQuery(id+"F5.boolean.opBoolean","SPLIT",EDGE,{"disambiguationData":[TD([makeQuery(id+"F5.opExtrude","SWEPT_FACE",FACE,{"disambiguationData":[OSD([sQuery(id+"F4.wireOp",EDGE,"E7.left")])]})])],"derivedFrom":makeQuery(id+"F1.opExtrude","SWEPT_EDGE",EDGE,{"disambiguationData":[OSD([subQ0,subQ1])]})});}
            var Q23;
            {var subQ0=sQuery(id+"F0.wireOp",EDGE,"E0.right");var subQ1=sQuery(id+"F0.wireOp",EDGE,"E0.bottom");var subQ2=makeQuery(id+"F1.opExtrude","SWEPT_EDGE",EDGE,{"disambiguationData":[OSD([subQ1,subQ0])]});Q23=makeQuery(id+"F7.boolean.opBoolean","COPY",EDGE,{"derivedFrom":makeQuery(id+"F7.opExtrude","CAP_EDGE",EDGE,{"disambiguationData":[OSD([subQ1,subQ0]),TDD([makeQuery(id+"F6.imprint","IMPRINT",EDGE,{"derivedFrom":makeQuery(id+"F5.boolean.opBoolean","COPY",EDGE,{"derivedFrom":makeQuery(id+"F5.opExtrude","CAP_EDGE",EDGE,{"disambiguationData":[OSD([subQ1,subQ0]),TDD([makeQuery(id+"F4.imprint","IMPRINT",EDGE,{"disambiguationData":[TD([[makeQuery(id+"F4.imprint","INTERSECT",VERTEX,{"derivedFrom":[subQ2,sQuery(id+"F4.wireOp",EDGE,"E6.top"),sQuery(id+"F4.wireOp",EDGE,"E6.right")]}),-1.0]])],"derivedFrom":subQ2})])],"isStart":false})})})])],"isStart":false})});}
            var Q24;
            {var subQ0=sQuery(id+"F0.wireOp",EDGE,"E0.bottom");var subQ1=sQuery(id+"F0.wireOp",EDGE,"E0.right");Q24=makeQuery(id+"F5.boolean.opBoolean","SPLIT",EDGE,{"disambiguationData":[TD([makeQuery(id+"F5.opExtrude","SWEPT_FACE",FACE,{"disambiguationData":[OSD([sQuery(id+"F4.wireOp",EDGE,"E6.left")])]})])],"derivedFrom":makeQuery(id+"F1.opExtrude","SWEPT_EDGE",EDGE,{"disambiguationData":[OSD([subQ0,subQ1])]})});}
            var Q25;
            {var subQ0=sQuery(id+"F0.wireOp",EDGE,"E0.right");var subQ1=sQuery(id+"F0.wireOp",EDGE,"E0.bottom");var subQ2=makeQuery(id+"F1.opExtrude","SWEPT_EDGE",EDGE,{"disambiguationData":[OSD([subQ1,subQ0])]});Q25=makeQuery(id+"F7.boolean.opBoolean","COPY",EDGE,{"derivedFrom":makeQuery(id+"F7.opExtrude","CAP_EDGE",EDGE,{"disambiguationData":[OSD([subQ1,subQ0]),TDD([makeQuery(id+"F6.imprint","IMPRINT",EDGE,{"derivedFrom":makeQuery(id+"F5.boolean.opBoolean","COPY",EDGE,{"derivedFrom":makeQuery(id+"F5.opExtrude","CAP_EDGE",EDGE,{"disambiguationData":[OSD([subQ1,subQ0]),TDD([makeQuery(id+"F4.imprint","IMPRINT",EDGE,{"disambiguationData":[TD([[makeQuery(id+"F4.imprint","INTERSECT",VERTEX,{"derivedFrom":[subQ2,sQuery(id+"F4.wireOp",EDGE,"E4")]}),-1.0]])],"derivedFrom":subQ2})])],"isStart":false})})})])],"isStart":false})});}
            var Q26;
            {var subQ0=sQuery(id+"F0.wireOp",EDGE,"E0.bottom");var subQ1=sQuery(id+"F0.wireOp",EDGE,"E0.right");Q26=makeQuery(id+"F5.boolean.opBoolean","SPLIT",EDGE,{"disambiguationData":[TD([makeQuery(id+"F5.opExtrude","SWEPT_FACE",FACE,{"disambiguationData":[OSD([sQuery(id+"F4.wireOp",EDGE,"E4")])]})])],"derivedFrom":makeQuery(id+"F1.opExtrude","SWEPT_EDGE",EDGE,{"disambiguationData":[OSD([subQ0,subQ1])]})});}
            var Q27;
            {var subQ0=sQuery(id+"F0.wireOp",EDGE,"E0.left");var subQ1=sQuery(id+"F0.wireOp",EDGE,"E0.bottom");Q27=makeQuery(id+"F7.boolean.opBoolean","SPLIT",EDGE,{"disambiguationData":[TD([makeQuery(id+"F5.boolean.opBoolean","COPY",FACE,{"derivedFrom":makeQuery(id+"F5.opExtrude","SWEPT_FACE",FACE,{"disambiguationData":[OSD([sQuery(id+"F4.wireOp",EDGE,"E5")])]})})])],"derivedFrom":makeQuery(id+"F1.opExtrude","SWEPT_EDGE",EDGE,{"disambiguationData":[OSD([subQ1,subQ0])]})});}
            var Q28;
            {var subQ0=sQuery(id+"F0.wireOp",EDGE,"E0.left");var subQ1=sQuery(id+"F0.wireOp",EDGE,"E0.bottom");var subQ2=makeQuery(id+"F1.opExtrude","SWEPT_EDGE",EDGE,{"disambiguationData":[OSD([subQ1,subQ0])]});Q28=makeQuery(id+"F9.boolean.opBoolean","COPY",EDGE,{"derivedFrom":makeQuery(id+"F9.opExtrude","CAP_EDGE",EDGE,{"disambiguationData":[OSD([subQ1,subQ0]),TDD([makeQuery(id+"F8.imprint","IMPRINT",EDGE,{"derivedFrom":makeQuery(id+"F7.boolean.opBoolean","COPY",EDGE,{"derivedFrom":makeQuery(id+"F7.opExtrude","CAP_EDGE",EDGE,{"disambiguationData":[OSD([subQ1,subQ0]),TDD([makeQuery(id+"F6.imprint","IMPRINT",EDGE,{"disambiguationData":[TD([[makeQuery(id+"F6.imprint","INTERSECT",VERTEX,{"derivedFrom":[subQ2,sQuery(id+"F6.wireOp",EDGE,"E14")]}),1.0]])],"derivedFrom":subQ2})])],"isStart":false})})})])],"isStart":false})});}
            var Q29;
            {var subQ0=sQuery(id+"F0.wireOp",EDGE,"E0.bottom");var subQ1=sQuery(id+"F0.wireOp",EDGE,"E0.left");Q29=makeQuery(id+"F7.boolean.opBoolean","SPLIT",EDGE,{"disambiguationData":[TD([makeQuery(id+"F7.opExtrude","SWEPT_FACE",FACE,{"disambiguationData":[OSD([sQuery(id+"F6.wireOp",EDGE,"E20.trimOffspring")])]})])],"derivedFrom":makeQuery(id+"F1.opExtrude","SWEPT_EDGE",EDGE,{"disambiguationData":[OSD([subQ0,subQ1])]})});}
            var Q30;
            {var subQ0=sQuery(id+"F0.wireOp",EDGE,"E0.left");var subQ1=sQuery(id+"F0.wireOp",EDGE,"E0.bottom");var subQ2=makeQuery(id+"F1.opExtrude","SWEPT_EDGE",EDGE,{"disambiguationData":[OSD([subQ1,subQ0])]});Q30=makeQuery(id+"F9.boolean.opBoolean","COPY",EDGE,{"derivedFrom":makeQuery(id+"F9.opExtrude","CAP_EDGE",EDGE,{"disambiguationData":[OSD([subQ1,subQ0]),TDD([makeQuery(id+"F8.imprint","IMPRINT",EDGE,{"derivedFrom":makeQuery(id+"F7.boolean.opBoolean","COPY",EDGE,{"derivedFrom":makeQuery(id+"F7.opExtrude","CAP_EDGE",EDGE,{"disambiguationData":[OSD([subQ1,subQ0]),TDD([makeQuery(id+"F6.imprint","IMPRINT",EDGE,{"disambiguationData":[TD([[makeQuery(id+"F6.imprint","INTERSECT",VERTEX,{"derivedFrom":[subQ2,sQuery(id+"F6.wireOp",EDGE,"E16.top"),sQuery(id+"F6.wireOp",EDGE,"E16.right")]}),-1.0]])],"derivedFrom":subQ2})])],"isStart":false})})})])],"isStart":false})});}
            var Q31;
            {var subQ0=sQuery(id+"F0.wireOp",EDGE,"E0.left");var subQ1=sQuery(id+"F0.wireOp",EDGE,"E0.bottom");Q31=makeQuery(id+"F7.boolean.opBoolean","SPLIT",EDGE,{"disambiguationData":[TD([makeQuery(id+"F5.boolean.opBoolean","COPY",FACE,{"derivedFrom":makeQuery(id+"F5.opExtrude","SWEPT_FACE",FACE,{"disambiguationData":[OSD([sQuery(id+"F4.wireOp",EDGE,"E7.left")])]})})])],"derivedFrom":makeQuery(id+"F1.opExtrude","SWEPT_EDGE",EDGE,{"disambiguationData":[OSD([subQ1,subQ0])]})});}
            var Q32;
            {var subQ0=sQuery(id+"F0.wireOp",EDGE,"E0.left");var subQ1=sQuery(id+"F0.wireOp",EDGE,"E0.bottom");var subQ2=makeQuery(id+"F1.opExtrude","SWEPT_EDGE",EDGE,{"disambiguationData":[OSD([subQ1,subQ0])]});Q32=makeQuery(id+"F9.boolean.opBoolean","COPY",EDGE,{"derivedFrom":makeQuery(id+"F9.opExtrude","CAP_EDGE",EDGE,{"disambiguationData":[OSD([subQ1,subQ0]),TDD([makeQuery(id+"F8.imprint","IMPRINT",EDGE,{"derivedFrom":makeQuery(id+"F7.boolean.opBoolean","COPY",EDGE,{"derivedFrom":makeQuery(id+"F7.opExtrude","CAP_EDGE",EDGE,{"disambiguationData":[OSD([subQ1,subQ0]),TDD([makeQuery(id+"F6.imprint","IMPRINT",EDGE,{"disambiguationData":[TD([[makeQuery(id+"F6.imprint","INTERSECT",VERTEX,{"derivedFrom":[subQ2,sQuery(id+"F6.wireOp",EDGE,"E15.top"),sQuery(id+"F6.wireOp",EDGE,"E15.right")]}),-1.0]])],"derivedFrom":subQ2})])],"isStart":false})})})])],"isStart":false})});}
            var Q33;
            {var subQ0=sQuery(id+"F0.wireOp",EDGE,"E0.left");var subQ1=sQuery(id+"F0.wireOp",EDGE,"E0.bottom");Q33=makeQuery(id+"F7.boolean.opBoolean","SPLIT",EDGE,{"disambiguationData":[TD([makeQuery(id+"F5.boolean.opBoolean","COPY",FACE,{"derivedFrom":makeQuery(id+"F5.opExtrude","SWEPT_FACE",FACE,{"disambiguationData":[OSD([sQuery(id+"F4.wireOp",EDGE,"E6.left")])]})})])],"derivedFrom":makeQuery(id+"F1.opExtrude","SWEPT_EDGE",EDGE,{"disambiguationData":[OSD([subQ1,subQ0])]})});}
            var Q34;
            {var subQ0=sQuery(id+"F0.wireOp",EDGE,"E0.left");var subQ1=sQuery(id+"F0.wireOp",EDGE,"E0.bottom");var subQ2=makeQuery(id+"F1.opExtrude","SWEPT_EDGE",EDGE,{"disambiguationData":[OSD([subQ1,subQ0])]});Q34=makeQuery(id+"F9.boolean.opBoolean","COPY",EDGE,{"derivedFrom":makeQuery(id+"F9.opExtrude","CAP_EDGE",EDGE,{"disambiguationData":[OSD([subQ1,subQ0]),TDD([makeQuery(id+"F8.imprint","IMPRINT",EDGE,{"derivedFrom":makeQuery(id+"F7.boolean.opBoolean","COPY",EDGE,{"derivedFrom":makeQuery(id+"F7.opExtrude","CAP_EDGE",EDGE,{"disambiguationData":[OSD([subQ1,subQ0]),TDD([makeQuery(id+"F6.imprint","IMPRINT",EDGE,{"disambiguationData":[TD([[makeQuery(id+"F6.imprint","INTERSECT",VERTEX,{"derivedFrom":[subQ2,sQuery(id+"F6.wireOp",EDGE,"E13")]}),-1.0]])],"derivedFrom":subQ2})])],"isStart":false})})})])],"isStart":false})});}
            var Q35;
            {var subQ0=sQuery(id+"F0.wireOp",EDGE,"E0.left");var subQ1=sQuery(id+"F0.wireOp",EDGE,"E0.bottom");Q35=makeQuery(id+"F7.boolean.opBoolean","SPLIT",EDGE,{"disambiguationData":[TD([makeQuery(id+"F5.boolean.opBoolean","COPY",FACE,{"derivedFrom":makeQuery(id+"F5.opExtrude","SWEPT_FACE",FACE,{"disambiguationData":[OSD([sQuery(id+"F4.wireOp",EDGE,"E4")])]})})])],"derivedFrom":makeQuery(id+"F1.opExtrude","SWEPT_EDGE",EDGE,{"disambiguationData":[OSD([subQ1,subQ0])]})});}
            fillet(context, id + "F12", {"entities" : qUnion([Q0, Q1, Q2, Q3, Q4, Q5, Q6, Q7, Q8, Q9, Q10, Q11, Q12, Q13, Q14, Q15, Q16, Q17, Q18, Q19, Q20, Q21, Q22, Q23, Q24, Q25, Q26, Q27, Q28, Q29, Q30, Q31, Q32, Q33, Q34, Q35]), "radius" : 0.3 * mm, "tangentPropagation" : true, "allowEdgeOverflow" : false});
        }
    });
